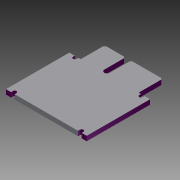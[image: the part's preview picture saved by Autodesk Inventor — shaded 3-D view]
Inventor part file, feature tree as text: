
AUTODESK INVENTOR PART (.ipt)
format: ipt  version: 2015 (Build 190159000, 159)  size: 187,392 bytes
history: native  units: in
note: dims shown in document units (in); Inventor stores cm internally (conversion verified against a paired STEP export)
features: extrude x2, sketch x2, shell x1
ambient origin geometry x8: Origin, YZ Plane, XZ Plane, XY Plane, X Axis, Y Axis, Z Axis, Center Point
bodies: Solid1 (feature_tree)
feature tree (5):
  extrude  "Extrusion1"  Depth=1.115in
  extrude  "Extrusion2"  Depth=0.925in
  shell  "Shell1"  Thickness=0.05in
  sketch  "Sketch1"  dims[d0=0.875in d1=1.115in]
  sketch  "Sketch2"  dims[d2=0.05in d3=0.095in d4=0.05in d5=0.025in d6=0.05in d7=0.05in d8=0.095in d9=0.025in d10=0.0646in d11=0.0in d12=0.05in d13=0.05in d14=0.05in d15=0.05in d16=0.1in d17=0.025in d18=0.1in d19=0.025in d20=0.8in d21=0.02in d22=0.02in d23=0.02in d24=0.02in d25=0.33in d26=0.075in d27=0.0375in d28=0.325in d29=0.02in d30=0.02in d31=0.02in d32=0.02in d33=0.1181in d34=0.0in d35=0.2756in d36=0.2362in d37=0.2362in d38=0.0394in d39=0.0197in d40=0.925in]
